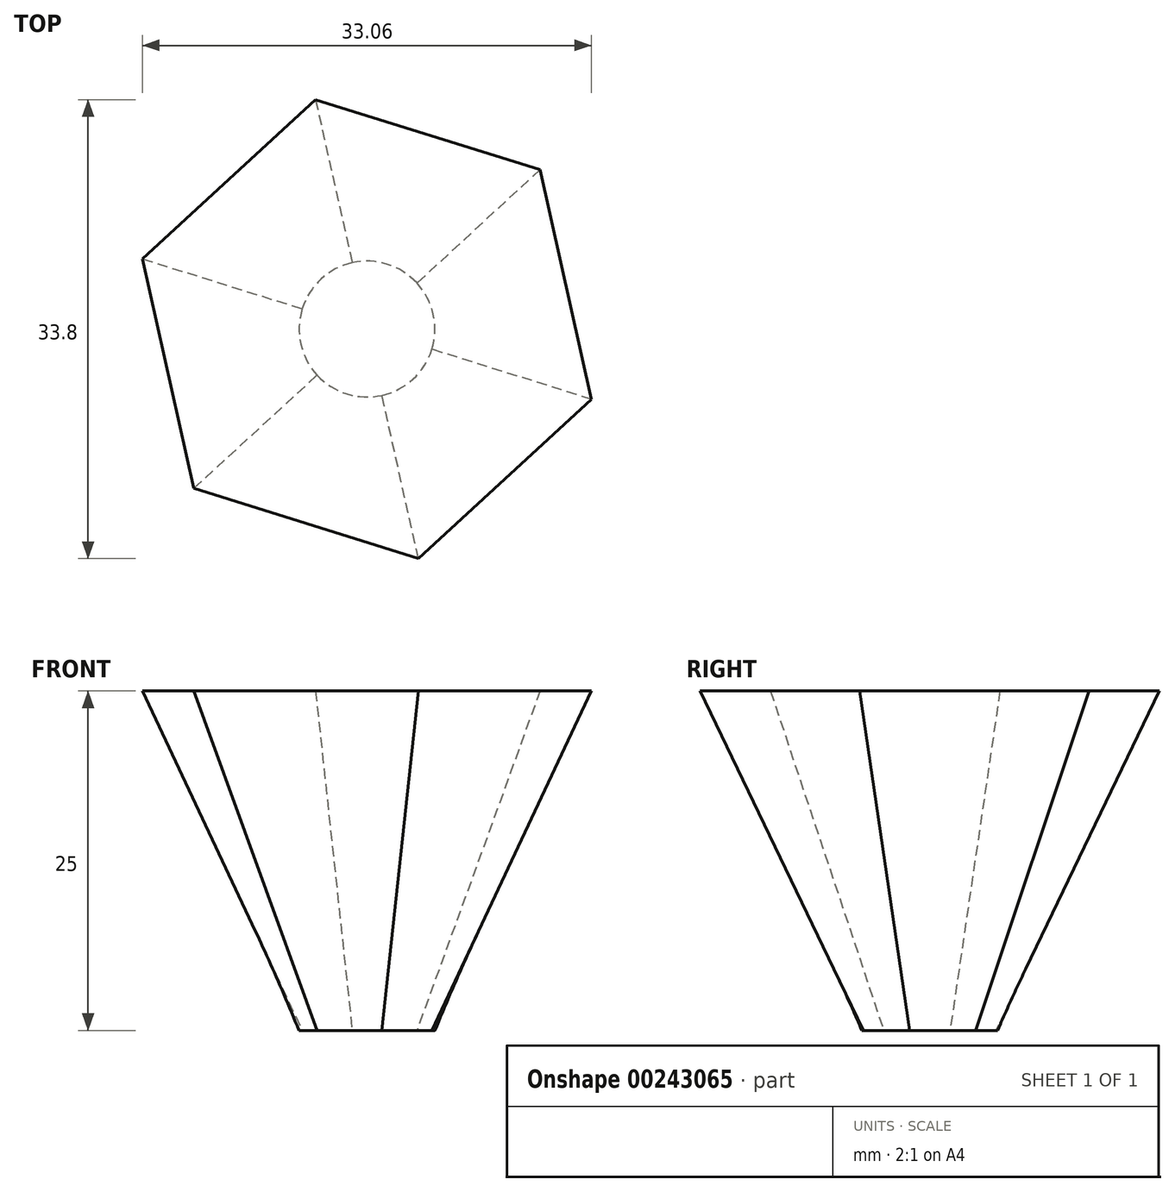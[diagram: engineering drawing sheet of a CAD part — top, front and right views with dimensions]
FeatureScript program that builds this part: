
annotation { "Feature Type Name" : "Feature", "Feature Type Description" : "" }
export const myFeature = defineFeature(function(context is Context, id is Id, definition is map)
    precondition{}
    {
        {
            var Q0;
            Q0=qCreatedBy(makeId("Top.planeOp"),FACE);
            var sketch = newSketch(context, id + "F0", { "sketchPlane" : qUnion([Q0])});
            skCircle(sketch, "E0", {"center": v(0, 0) * mm, "radius": 5 * mm});
            skSolve(sketch);
        }
        {
            var Q0;
            Q0=qCreatedBy(makeId("Top.planeOp"),FACE);
            cPlane(context, id + "F1", {"entities" : qUnion([Q0]), "cplaneType" : CPlaneType.OFFSET, "offset" : 25 * mm, "width" : 150 * mm, "height" : 150 * mm});
        }
        {
            var Q0;
            Q0=qCreatedBy(id+"F1.planeOp",FACE);
            var sketch = newSketch(context, id + "F2", { "sketchPlane" : qUnion([Q0])});
            skCircle(sketch, "E1.cCircle", {"center": v(0, 0) * mm, "radius": 15 * mm, "construction": true});
            skLineSegment(sketch, "E1.0", {"start": v(3.79, -16.9) * mm, "end": v(-12.74, -11.73) * mm});
            skLineSegment(sketch, "E1.1", {"start": v(-12.74, -11.73) * mm, "end": v(-16.53, 5.17) * mm});
            skLineSegment(sketch, "E1.2", {"start": v(-16.53, 5.17) * mm, "end": v(-3.79, 16.9) * mm});
            skLineSegment(sketch, "E1.3", {"start": v(-3.79, 16.9) * mm, "end": v(12.74, 11.73) * mm});
            skLineSegment(sketch, "E1.4", {"start": v(12.74, 11.73) * mm, "end": v(16.53, -5.17) * mm});
            skLineSegment(sketch, "E1.5", {"start": v(16.53, -5.17) * mm, "end": v(3.79, -16.9) * mm});
            skPoint(sketch, "E1.0.midPoint", {"position": v(-4.48, -14.32) * mm});
            skSolve(sketch);
        }
        {
            var Q0;
            Q0=makeQuery(id+"F2.imprint","IMPRINT",FACE,{"disambiguationData":[TD([[makeQuery(id+"F2.imprint","IMPRINT",EDGE,{"derivedFrom":sQuery(id+"F2.wireOp",EDGE,"E1.0")}),-1.0]])]});
            var Q1;
            Q1=makeQuery(id+"F0.imprint","IMPRINT",FACE,{"disambiguationData":[TD([[makeQuery(id+"F0.imprint","IMPRINT",EDGE,{"derivedFrom":sQuery(id+"F0.wireOp",EDGE,"E0")}),1.0]])]});
            loft(context, id + "F3", {"sheetProfilesArray" : [{ "sheetProfileEntities" : qUnion([Q0]) }, { "sheetProfileEntities" : qUnion([Q1]) }]});
        }
    });
